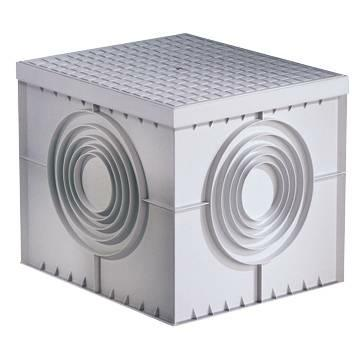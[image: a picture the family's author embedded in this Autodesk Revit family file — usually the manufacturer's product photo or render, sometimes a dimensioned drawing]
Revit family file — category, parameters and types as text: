
# Revit family: Building-Conduits-GEWISS-PU-ACCESS-CHAMBER-THERMOPLASTIC_SQUARE
name_source: partatom
category: Attrezzatura elettrica
revit_build: Autodesk Revit 2016 (Build: 20161004_0715(x64)
units: mm (PartAtom-declared; Revit-internal decimal feet)

## family parameters
Condiviso = No
Configurazione quadro = Due colonne, circuiti in orizzontale
Host = Superficie
Numero OmniClass = 23.80.30.00
Punto di calcolo locali = Sì
Quota connettore circolare = Usa diametro
Taglio con vuoti quando caricato = No
Tipo di parte = Pannello comandi
Titolo OmniClass = Distribution Devices

## types (8) — shared parameters
Bordo acceso = Sì
Catalogue = BUILDING
Catalogue Range = PU
Colour = Grey
Electrocod = 210
Finitura pozzetto = <Per categoria>
IDF = 7d80b8f5-db45-42b8-bc80-d20d9b467a1b
IDT = 652dbf2e-3665-4c45-83b8-61deb2828763
Immagine tipo = DX59902.jpg
Incasso pozzetto = 520 mm  [stored 1.70604 ft]
Larghezza_pozzetto = 550 mm
Lunghezza pozzetto = 550 mm
Produttore = GEWISS S.p.A.
Prospetto di default = 1219 mm
SEO = Well
Simbolo acceso = Sì
Technical sheet = https://www.gewiss.com
URL = https://www.gewiss.com
Version file RFA = 18.0

## per-type parameters (varying)
| type | Characteristics | Descrizione | Dimension | Dimensions (mm) | EAN code | Modello |
| DX59402 - 200X200 ACCESS CHAMBER WITHOUT LID | Flat semi-pierced base for boosting | 200X200 ACCESS CHAMBER WITHOUT LID | 200x200x200 mm | 200x200x200 mm | 8011564131026 | DX59402 |
| DX59902 - 500X500 ACCESS CHAMBER WITHOUT LID | Flat semi-pierced base for boosting | 500X500 ACCESS CHAMBER WITHOUT LID | 550x550x520 mm | 550x550x520 mm | 8011564131323 | DX59902 |
| DX59702 - 300X300 ACCESS CHAMBER WITHOUT LID | Flat semi-pierced base for boosting | 300X300 ACCESS CHAMBER WITHOUT LID | 300x300x300 mm | 300x300x300 mm | 8011564131170 | DX59702 |
| DX59701 - 300X300 ACCESS CHAMBER | Flat knockout base and high resistance lid | 300X300 ACCESS CHAMBER | 300x300x300 mm | 300x300x300 mm | 8011564131163 | DX59701 |
| DX59802 - 400X400 ACCESS CHAMBER WITHOUT LID | Flat semi-pierced base for boosting | 400X400 ACCESS CHAMBER WITHOUT LID | 400x400x400 mm | 400x400x400 mm | 8011564131248 | DX59802 |
| DX59801 - 400X400 ACCESS CHAMBER | Flat knockout base and high resistance lid | 400X400 ACCESS CHAMBER | 400x400x400 mm | 400x400x400 mm | 8011564131231 | DX59801 |
| DX59901 - 500X500 ACCESS CHAMBER | Flat knockout base and high resistance lid | 500X500 ACCESS CHAMBER | 550x550x520 mm | 550x550x520 mm | 8011564131316 | DX59901 |
| DX59401 - 200X200 ACCESS CHAMBER | Flat knockout base and high resistance lid | 200X200 ACCESS CHAMBER | 200x200x200 mm | 200x200x200 mm | 8011564131019 | DX59401 |

note: [stored X ft] marks values corroborated as IEEE doubles in the binary element streams (Revit-internal decimal feet)

## geometry (parser evidence)
native form markers: Sweep x2
no freeform markers — native parametric forms only
